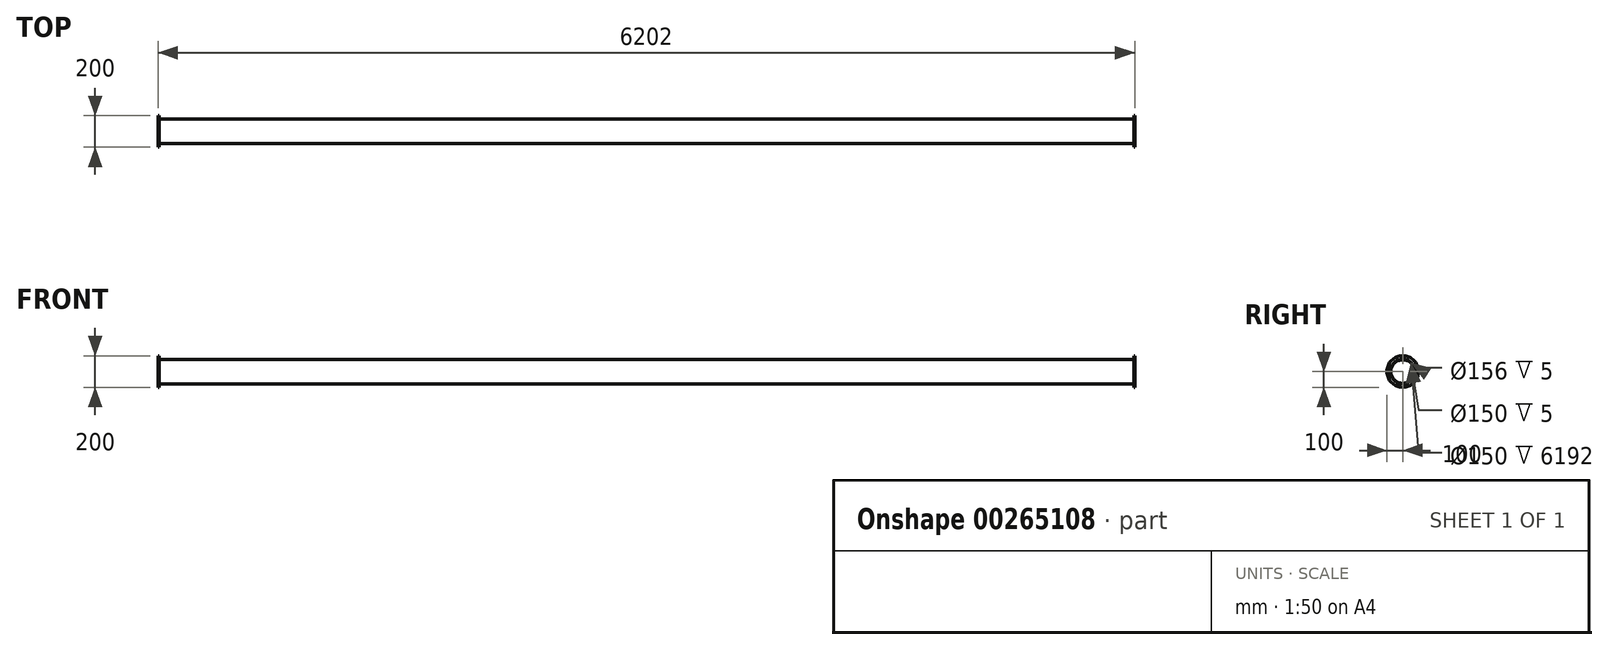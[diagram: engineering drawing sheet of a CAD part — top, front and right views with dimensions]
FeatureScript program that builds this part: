
annotation { "Feature Type Name" : "Feature", "Feature Type Description" : "" }
export const myFeature = defineFeature(function(context is Context, id is Id, definition is map)
    precondition{}
    {
        {
            var Q0;
            Q0=qCreatedBy(makeId("Front.planeOp"),FACE);
            var sketch = newSketch(context, id + "F0", { "sketchPlane" : qUnion([Q0])});
            skLineSegment(sketch, "E0", {"start": v(0, 0) * mm, "end": v(-6192, 0) * mm, "construction": true});
            skLineSegment(sketch, "E1.bottom", {"start": v(0, 78) * mm, "end": v(-6192, 78) * mm});
            skLineSegment(sketch, "E1.top", {"start": v(0, 75) * mm, "end": v(-6192, 75) * mm});
            skLineSegment(sketch, "E1.left", {"start": v(0, 78) * mm, "end": v(0, 75) * mm});
            skLineSegment(sketch, "E1.right", {"start": v(-6192, 78) * mm, "end": v(-6192, 75) * mm});
            skSolve(sketch);
        }
        {
            var Q0;
            Q0=makeQuery(id+"F0.imprint","IMPRINT",FACE,{"disambiguationData":[TD([[makeQuery(id+"F0.imprint","IMPRINT",EDGE,{"derivedFrom":sQuery(id+"F0.wireOp",EDGE,"E1.bottom")}),1.0]])]});
            var Q1;
            Q1=sQuery(id+"F0.wireOp",EDGE,"E0");
            revolve(context, id + "F1", {"entities" : qUnion([Q0]), "axis" : qUnion([Q1]), "revolveType" : RevolveType.FULL});
        }
        {
            var Q0;
            Q0=makeQuery(id+"F1.opRevolve","SWEPT_FACE",FACE,{"disambiguationData":[OSD([sQuery(id+"F0.wireOp",EDGE,"E1.right")])]});
            var sketch = newSketch(context, id + "F2", { "sketchPlane" : qUnion([Q0])});
            skCircle(sketch, "E2", {"center": v(0, 0) * mm, "radius": 75 * mm});
            skCircle(sketch, "E3", {"center": v(0, 0) * mm, "radius": 100 * mm});
            skSolve(sketch);
        }
        {
            var Q0;
            Q0=makeQuery(id+"F2.imprint","IMPRINT",FACE,{"disambiguationData":[TD([[makeQuery(id+"F2.imprint","IMPRINT",EDGE,{"derivedFrom":sQuery(id+"F2.wireOp",EDGE,"E3")}),1.0]])]});
            var Q1;
            Q1=makeQuery(id+"F2.imprint","IMPRINT",FACE,{"disambiguationData":[TD([[makeQuery(id+"F2.imprint","IMPRINT",EDGE,{"derivedFrom":sQuery(id+"F2.wireOp",EDGE,"E2")}),1.0]])]});
            extrude(context, id + "F3", {"entities" : qUnion([Q0, Q1]), "depth" : 5 * mm});
        }
        {
            var Q0;
            Q0=makeQuery(id+"F1.opRevolve","SWEPT_FACE",FACE,{"disambiguationData":[OSD([sQuery(id+"F0.wireOp",EDGE,"E1.left")])]});
            var sketch = newSketch(context, id + "F4", { "sketchPlane" : qUnion([Q0])});
            skCircle(sketch, "E4", {"center": v(0, 0) * mm, "radius": 100 * mm});
            skCircle(sketch, "E5", {"center": v(0, 0) * mm, "radius": 75 * mm});
            skSolve(sketch);
        }
        {
            var Q0;
            Q0=makeQuery(id+"F4.imprint","IMPRINT",FACE,{"disambiguationData":[TD([[makeQuery(id+"F4.imprint","IMPRINT",EDGE,{"derivedFrom":sQuery(id+"F4.wireOp",EDGE,"E4")}),1.0]])]});
            extrude(context, id + "F5", {"entities" : qUnion([Q0]), "depth" : 5 * mm});
        }
    });
